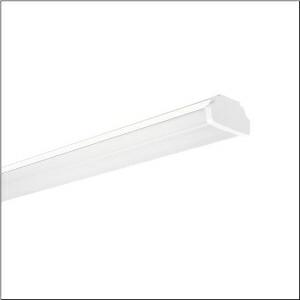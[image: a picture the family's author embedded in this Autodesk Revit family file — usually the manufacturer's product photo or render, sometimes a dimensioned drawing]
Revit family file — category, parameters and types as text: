
# Revit family: modario_r__31_ho_53bm812c1v4105_deab
name_source: partatom
category: Lighting Fixtures
units: mm (PartAtom-declared; Revit-internal decimal feet)

## family parameters
Cut with Voids When Loaded = No
Host = Face
Light Source = No
Part Type = Normal
Room Calculation Point = No
Round Connector Dimension = Use Diameter
Shared = No

## types (1)
- --- (1 x LED, 10520 lm, 63.8 W, 4000K)
    Apparent Load = 64 VA
    CIE Flux Codes = 47 80 95 92 100
    Color Rendering = 80
    Color Temperature = 4000K
    Default Elevation = 1800 mm
    Description = Modario® 31 HO, luminaire insert, of sheet steel, coil coated, white, length: 1.495mm, width: 81mm, height: 82mm, 5x system unit, system units: 299mm, LED rated luminous flux: 10.520lm, light colour: 840, control gear: ON/OFF Multilumen, CLOi, control gear: ECG Multilumen, with plug, 3-pole, with phase selection, mains connection: 220..240V, AC, 50/60Hz, start of lifetime: 64W, end of service life: 73W, through-wiring accessed according to module size, primary optical cover: cover, of PMMA, light emission: direct distribution, primary light characteristic: symmetric, protection rating (complete): IP20, protection rating (LED compartment): IP50, insulation class (complete): insulation class I (protective earthing), certification: CE, ENEC, VDE, UKCA, impact resistance: IK03, permissible ambient temperature for indoor applications: -35..+35°C, corresponds to IFS (International Featured Standards) requirements for safety and quality in the food industry, reducing of maximum allowable ambient temperature of 5°C with ceiling mounting, packaging unit: 1 piece
    Height = 92 mm
    Lamp = 1 x LED
    Lamp Light Flux = 10520 lm
    Lamp Power = 63.8 W
    Lamp count = 1
    Length = 1495 mm
    Luminous efficacy = 165 lm/W
    Manufacturer = Siteco
    ModVariant = No
    Model = 53BM812C1V4105
    Mounting Place = Ceiling
    Mounting Type = Pendant
    Number of Poles = 1
    OnlyDefault = Yes
    Power Factor = 1
    Product Name = Modario® 31 HO
    Product group = luminaire insert | ceiling pendant
    ProductGroupID = 902
    Protection Class = Protection class I
    Protection Degree = IP 20
    RLX_Detail_Level = 1
    RLX_Emergency_Light_Flux = 0 lm
    RLX_Emergency_Type = 0
    RLX_Emergency_Type_DB = No
    RlxData = <blob elided: 40085 chars, md5=ad88ec92>
    Socket = socket
    Standby Power = 0 W
    System Light Flux = 10520 lm
    System Power = 64 W
    Type Comments = factory setting: luminous flux: 100 % | (A | C | E) | 144 mA
    Type Image = l_1341886.jpg
    URL = http://relux.com
    VarID = @adj_219521
    Voltage = 0 V
    Weight = 0.00 kg
    Width = 81 mm

## geometry (parser evidence)
native form markers: Blend x4, Sweep x13
no freeform markers — native parametric forms only
